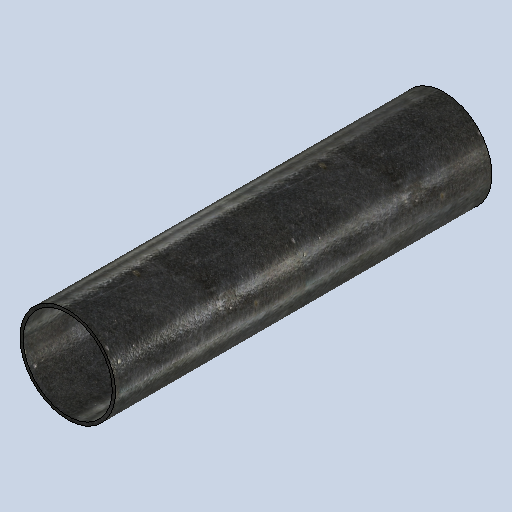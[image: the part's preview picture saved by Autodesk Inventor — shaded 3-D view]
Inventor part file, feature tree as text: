
AUTODESK INVENTOR PART (.ipt)
format: ipt  version: 2025 (Build 290162010, 162A)  size: 224,768 bytes
history: native  units: mm
features: extrude x1, sketch x1
ambient origin geometry x8: Origin, YZ Plane, XZ Plane, XY Plane, X Axis, Y Axis, Z Axis, Center Point
bodies: Solid1 (feature_tree)
feature tree (2):
  extrude  "Extrusion1"  Depth=355.0mm
  sketch  "Sketch1"  dims[d0=90.0mm d1=3.0mm d2=355.0mm d3=0.0mm]
